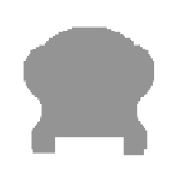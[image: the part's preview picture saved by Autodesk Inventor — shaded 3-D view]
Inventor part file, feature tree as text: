
AUTODESK INVENTOR PART (.ipt)
format: ipt  version: 2019 (Build 230136000, 136)  size: 150,016 bytes
history: native  units: mm
features: other x11, sketch x1, extrude x1
ambient origin geometry x8: Origin, YZ Plane, XZ Plane, XY Plane, X Axis, Y Axis, Z Axis, Center Point
bodies: Body1 (feature_tree)
feature tree (13):
  other  "Твердое тело1"
  other  "Блоки"
  sketch  "Эскиз"
  other  "Начальная плоскость"
  other  "РабПлоскость2"
  extrude  "Тело"  [1 undecoded]
  other  "Конечная плоскость"
  other  "РабПлоскость4"
  other  "Разделение1"
  other  "РабПлоскость5"
  other  "Разделение2"
  other  "Поручень"
  other  "Поручень:1"
note: 1 required parameter value undecoded (feature->parameter linkage not recoverable at this tier; creation-order binding heuristic only, values carry confidence <= 0.55)
